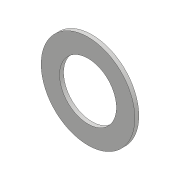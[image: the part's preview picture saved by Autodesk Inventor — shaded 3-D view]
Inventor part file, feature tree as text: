
AUTODESK INVENTOR PART (.ipt)
format: ipt  version: 2018 (Build 220112000, 112)  size: 80,896 bytes
history: native  units: mm
features: extrude x1, sketch x1
ambient origin geometry x8: Origin, YZ Plane, XZ Plane, XY Plane, X Axis, Y Axis, Z Axis, Center Point
bodies: Solid1 (feature_tree)
feature tree (2):
  extrude  "Extrusion1"  Depth=0.6mm
  sketch  "Sketch1"  dims[d0=8.5mm d1=14.0mm d2=0.6mm d3=0.0mm]
